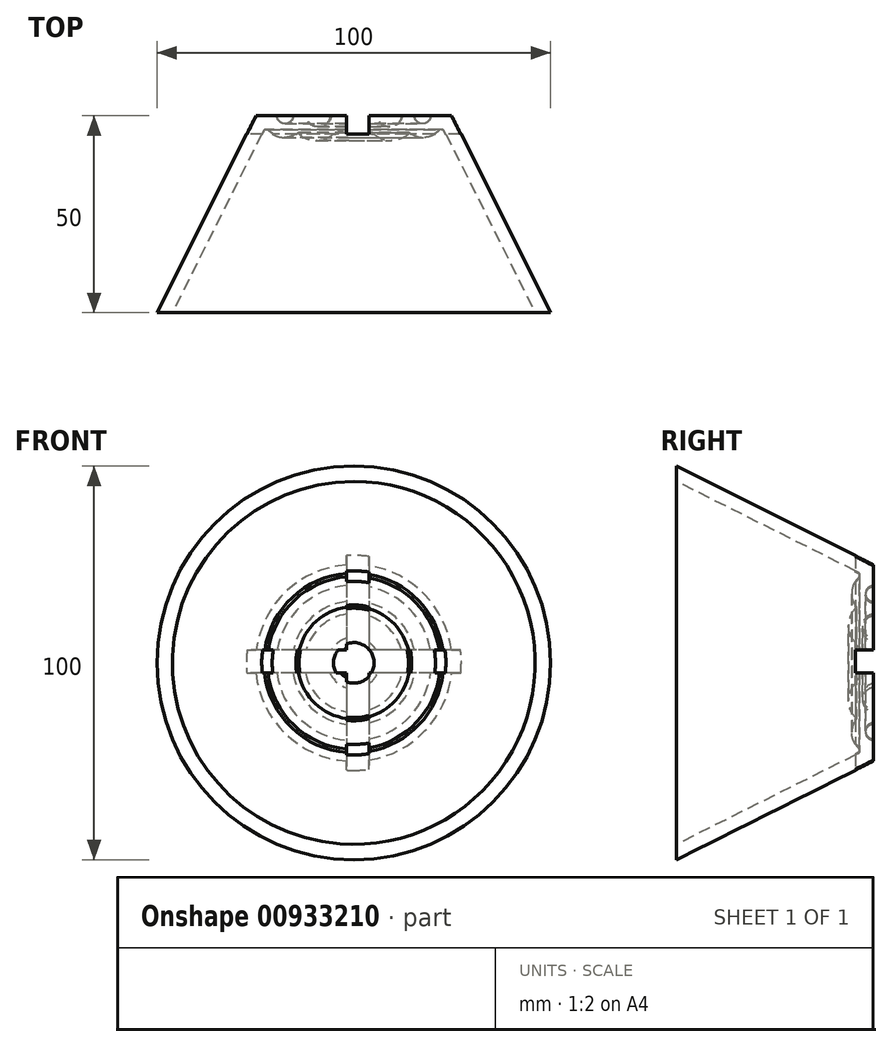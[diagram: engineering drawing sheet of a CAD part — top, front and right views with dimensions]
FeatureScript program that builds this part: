
annotation { "Feature Type Name" : "Feature", "Feature Type Description" : "" }
export const myFeature = defineFeature(function(context is Context, id is Id, definition is map)
    precondition{}
    {
        {
            var Q0;
            Q0=qCreatedBy(makeId("Top.planeOp"),FACE);
            var sketch = newSketch(context, id + "F0", { "sketchPlane" : qUnion([Q0])});
            skLineSegment(sketch, "E0", {"start": v(0, 0) * mm, "end": v(0, 50) * mm});
            skLineSegment(sketch, "E1", {"start": v(-25, 50) * mm, "end": v(-50, 0) * mm});
            skLineSegment(sketch, "E2", {"start": v(-50, 0) * mm, "end": v(0, 0) * mm});
            skArc(sketch, "E3", {"start": v(-19.71, 50) * mm, "mid": v(-17.71, 48) * mm, "end": v(-15.71, 50) * mm});
            skArc(sketch, "E4", {"start": v(-12.53, 50) * mm, "mid": v(-9.53, 47.2) * mm, "end": v(-6.54, 50) * mm});
            skLineSegment(sketch, "E5", {"start": v(-25, 50) * mm, "end": v(-19.71, 50) * mm});
            skLineSegment(sketch, "E6", {"start": v(-15.71, 50) * mm, "end": v(-12.53, 50) * mm});
            skLineSegment(sketch, "E7", {"start": v(-6.54, 50) * mm, "end": v(-4.76, 50) * mm});
            skLineSegment(sketch, "E8", {"start": v(0, 50) * mm, "end": v(-4.76, 50) * mm});
            skSolve(sketch);
        }
        {
            var Q0;
            {var subQ3=sQuery(id+"F0.wireOp",EDGE,"E0");Q0=makeQuery(id+"F0.imprint","IMPRINT",FACE,{"disambiguationData":[TD([[makeQuery(id+"F0.imprint","IMPRINT",EDGE,{"derivedFrom":subQ3}),1.0]])]});}
            var Q1;
            Q1=sQuery(id+"F0.wireOp",EDGE,"E0");
            revolve(context, id + "F1", {"surfaceOperationType" : NewSurfaceOperationType.NEW, "entities" : qUnion([Q0]), "axis" : qUnion([Q1]), "revolveType" : RevolveType.FULL});
        }
        {
            var Q0;
            Q0=makeQuery(id+"F1.opRevolve","SWEPT_FACE",FACE,{"disambiguationData":[OSD([sQuery(id+"F0.wireOp",EDGE,"E2")])]});
            shell(context, id + "F2", {"entities" : qUnion([Q0]), "thickness" : 3.5 * mm});
        }
        {
            var Q0;
            Q0=makeQuery(id+"F1.opRevolve","SWEPT_FACE",FACE,{"disambiguationData":[OSD([sQuery(id+"F0.wireOp",EDGE,"E8")])]});
            var sketch = newSketch(context, id + "F3", { "sketchPlane" : qUnion([Q0])});
            skLineSegment(sketch, "E9.bottom", {"start": v(-49.39, 3.27) * mm, "end": v(50.06, 3.27) * mm});
            skLineSegment(sketch, "E9.top", {"start": v(-49.39, -2.59) * mm, "end": v(50.06, -2.59) * mm});
            skLineSegment(sketch, "E9.left", {"start": v(-49.39, 3.27) * mm, "end": v(-49.39, -2.59) * mm});
            skLineSegment(sketch, "E9.right", {"start": v(50.06, 3.27) * mm, "end": v(50.06, -2.59) * mm});
            skLineSegment(sketch, "E10.bottom", {"start": v(-3.92, 49.71) * mm, "end": v(1.8, 49.71) * mm});
            skLineSegment(sketch, "E10.top", {"start": v(-3.92, -49.87) * mm, "end": v(1.8, -49.87) * mm});
            skLineSegment(sketch, "E10.left", {"start": v(-3.92, 49.71) * mm, "end": v(-3.92, -49.87) * mm});
            skLineSegment(sketch, "E10.right", {"start": v(1.8, 49.71) * mm, "end": v(1.8, -49.87) * mm});
            skSolve(sketch);
        }
        {
            var Q0;
            Q0 = qSketchRegion(id + "F3", true);
            extrude(context, id + "F4", {"entities" : qUnion([Q0]), "operationType" : NewBodyOperationType.REMOVE, "oppositeDirection" : true, "depth" : 4.6 * mm, "offsetDistance" : 25 * mm});
        }
    });
